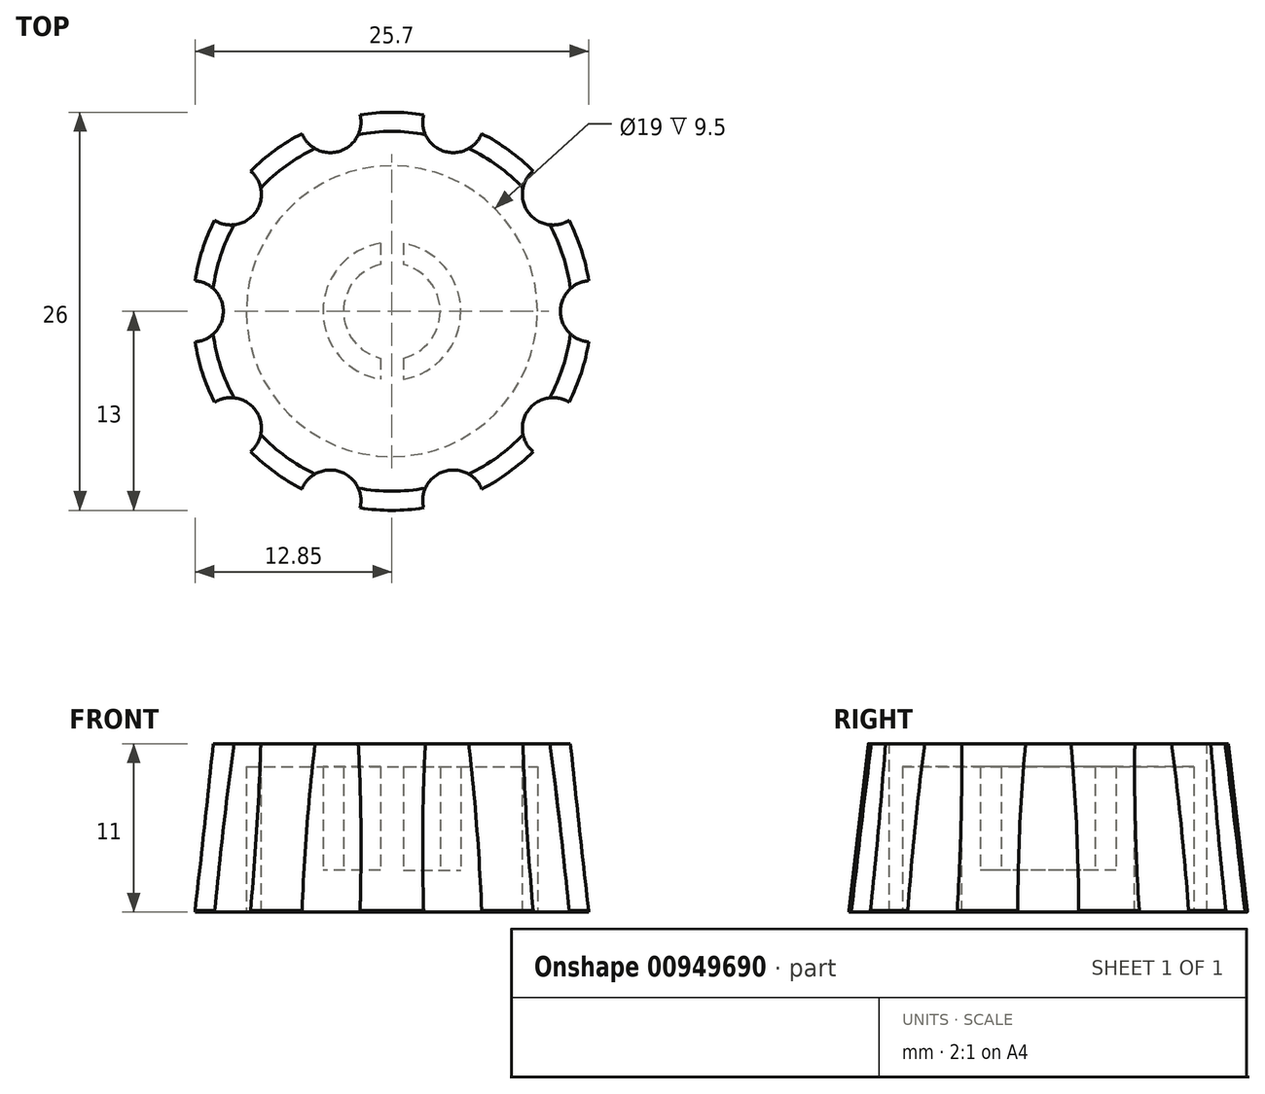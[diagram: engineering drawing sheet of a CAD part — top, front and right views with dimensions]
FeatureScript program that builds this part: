
annotation { "Feature Type Name" : "Feature", "Feature Type Description" : "" }
export const myFeature = defineFeature(function(context is Context, id is Id, definition is map)
    precondition{}
    {
        {
            var Q0;
            Q0=qCreatedBy(makeId("Top.planeOp"),FACE);
            var sketch = newSketch(context, id + "F0", { "sketchPlane" : qUnion([Q0])});
            skCircle(sketch, "E0", {"center": v(0, 0) * mm, "radius": 13 * mm});
            skCircle(sketch, "E1", {"center": v(0, 0) * mm, "radius": 3.15 * mm});
            skCircle(sketch, "E2", {"center": v(0, 0) * mm, "radius": 11.75 * mm});
            skSolve(sketch);
        }
        {
            var Q0;
            Q0=qCreatedBy(makeId("Top.planeOp"),FACE);
            cPlane(context, id + "F1", {"entities" : qUnion([Q0]), "cplaneType" : CPlaneType.OFFSET, "offset" : 11 * mm, "width" : 150 * mm, "height" : 150 * mm});
        }
        {
            var Q0;
            Q0=qCreatedBy(id+"F1.planeOp",FACE);
            var sketch = newSketch(context, id + "F2", { "sketchPlane" : qUnion([Q0])});
            skCircle(sketch, "E3.0", {"center": v(0, 0) * mm, "radius": 11.75 * mm});
            skSolve(sketch);
        }
        {
            var Q0;
            Q0=makeQuery(id+"F0.imprint","IMPRINT",FACE,{"disambiguationData":[TD([[makeQuery(id+"F0.imprint","IMPRINT",EDGE,{"derivedFrom":sQuery(id+"F0.wireOp",EDGE,"E0")}),1.0]])]});
            var Q1;
            Q1=makeQuery(id+"F0.imprint","IMPRINT",FACE,{"disambiguationData":[TD([[makeQuery(id+"F0.imprint","IMPRINT",EDGE,{"derivedFrom":sQuery(id+"F0.wireOp",EDGE,"E1")}),-1.0]])]});
            var Q2;
            Q2=makeQuery(id+"F0.imprint","IMPRINT",FACE,{"disambiguationData":[TD([[makeQuery(id+"F0.imprint","IMPRINT",EDGE,{"derivedFrom":sQuery(id+"F0.wireOp",EDGE,"E1")}),1.0]])]});
            extrude(context, id + "F3", {"entities" : qUnion([Q0, Q1, Q2]), "depth" : 0.1 * mm, "offsetDistance" : 25 * mm});
        }
        {
            var Q1;
            Q1=makeQuery(id+"F3.opExtrude","CAP_FACE",FACE,{"disambiguationData":[OSD([sQuery(id+"F0.wireOp",EDGE,"E0")])],"isStart":false});
            var Q2;
            Q2=makeQuery(id+"F2.imprint","IMPRINT",FACE,{"disambiguationData":[TD([[makeQuery(id+"F2.imprint","IMPRINT",EDGE,{"derivedFrom":sQuery(id+"F2.wireOp",EDGE,"E3.0")}),1.0]])]});
            loft(context, id + "F4", {"operationType" : NewBodyOperationType.ADD, "sheetProfilesArray" : [{ "sheetProfileEntities" : qUnion([Q1]) }, { "sheetProfileEntities" : qUnion([Q2]) }]});
        }
        {
            var Q0;
            Q0=makeQuery(id+"F0.imprint","IMPRINT",FACE,{"disambiguationData":[TD([[makeQuery(id+"F0.imprint","IMPRINT",EDGE,{"derivedFrom":sQuery(id+"F0.wireOp",EDGE,"E1")}),1.0]])]});
            extrude(context, id + "F5", {"entities" : qUnion([Q0]), "operationType" : NewBodyOperationType.REMOVE, "depth" : 9.5 * mm, "offsetDistance" : 25 * mm});
        }
        {
            var Q0;
            Q0=makeQuery(id+"F4.opLoft","CAP_FACE",FACE,{"disambiguationData":[OSD([makeQuery(id+"F2.imprint","IMPRINT",FACE,{"disambiguationData":[TD([[makeQuery(id+"F2.imprint","IMPRINT",EDGE,{"derivedFrom":sQuery(id+"F2.wireOp",EDGE,"E3.0")}),1.0]])]})])],"isStart":true});
            var sketch = newSketch(context, id + "F6", { "sketchPlane" : qUnion([Q0])});
            skCircle(sketch, "E4.0", {"center": v(0, 0) * mm, "radius": 13 * mm, "construction": true});
            skCircle(sketch, "E5", {"center": v(13, 0) * mm, "radius": 2 * mm});
            skCircle(sketch, "E6.1.0", {"center": v(10.52, 7.64) * mm, "radius": 2 * mm});
            skCircle(sketch, "E6.2.0", {"center": v(4.02, 12.36) * mm, "radius": 2 * mm});
            skCircle(sketch, "E6.3.0", {"center": v(-4.02, 12.36) * mm, "radius": 2 * mm});
            skCircle(sketch, "E6.4.0", {"center": v(-10.52, 7.64) * mm, "radius": 2 * mm});
            skCircle(sketch, "E6.5.0", {"center": v(-13, 0) * mm, "radius": 2 * mm});
            skCircle(sketch, "E6.6.0", {"center": v(-10.52, -7.64) * mm, "radius": 2 * mm});
            skCircle(sketch, "E6.7.0", {"center": v(-4.02, -12.36) * mm, "radius": 2 * mm});
            skCircle(sketch, "E6.8.0", {"center": v(4.02, -12.36) * mm, "radius": 2 * mm});
            skCircle(sketch, "E6.9.0", {"center": v(10.52, -7.64) * mm, "radius": 2 * mm});
            skSolve(sketch);
        }
        {
            var Q0;
            Q0 = qSketchRegion(id + "F6", true);
            extrude(context, id + "F7", {"entities" : qUnion([Q0]), "operationType" : NewBodyOperationType.REMOVE, "oppositeDirection" : true, "depth" : 25 * mm, "offsetDistance" : 25 * mm});
        }
        {
            var Q0;
            Q0 = qSketchRegion(id + "F6", true);
            extrude(context, id + "F8", {"entities" : qUnion([Q0]), "operationType" : NewBodyOperationType.REMOVE, "endBound" : BoundingType.THROUGH_ALL, "oppositeDirection" : true, "depth" : 4 * mm, "offsetDistance" : 25 * mm});
        }
        {
            var Q0;
            Q0=makeQuery(id+"F3.opExtrude","CAP_FACE",FACE,{"disambiguationData":[OSD([sQuery(id+"F0.wireOp",EDGE,"E0")])],"isStart":true});
            var sketch = newSketch(context, id + "F9", { "sketchPlane" : qUnion([Q0])});
            skCircle(sketch, "E7", {"center": v(0, 0) * mm, "radius": 9.5 * mm});
            skArc(sketch, "E8", {"start": v(0.75, -4.44) * mm, "mid": v(4.5, 0) * mm, "end": v(0.75, 4.44) * mm});
            skArc(sketch, "E9.0", {"start": v(0.75, -3.06) * mm, "mid": v(3.15, 0) * mm, "end": v(0.75, 3.06) * mm});
            skLineSegment(sketch, "E10.left", {"start": v(0.75, -4.44) * mm, "end": v(0.75, -3.06) * mm});
            skLineSegment(sketch, "E10.right", {"start": v(-0.75, -4.44) * mm, "end": v(-0.75, -3.06) * mm});
            skLineSegment(sketch, "E11.trimOffspring", {"start": v(0.75, 3.06) * mm, "end": v(0.75, 4.44) * mm});
            skLineSegment(sketch, "E12.trimOffspring", {"start": v(-0.75, 3.06) * mm, "end": v(-0.75, 4.44) * mm});
            skArc(sketch, "E13.trimOffspring", {"start": v(-0.75, 3.06) * mm, "mid": v(-3.15, 0) * mm, "end": v(-0.75, -3.06) * mm});
            skArc(sketch, "E14.trimOffspring", {"start": v(-0.75, 4.44) * mm, "mid": v(-4.5, 0) * mm, "end": v(-0.75, -4.44) * mm});
            skArc(sketch, "E15.0", {"start": v(-0.75, -3.06) * mm, "mid": v(0, -3.15) * mm, "end": v(0.75, -3.06) * mm});
            skArc(sketch, "E16.trimOffspring", {"start": v(0.75, 3.06) * mm, "mid": v(0, 3.15) * mm, "end": v(-0.75, 3.06) * mm});
            skSolve(sketch);
        }
        {
            var Q0;
            Q0=makeQuery(id+"F9.imprint","IMPRINT",FACE,{"disambiguationData":[TD([[makeQuery(id+"F9.imprint","IMPRINT",EDGE,{"derivedFrom":sQuery(id+"F9.wireOp",EDGE,"E7")}),1.0]])]});
            extrude(context, id + "F10", {"entities" : qUnion([Q0]), "operationType" : NewBodyOperationType.REMOVE, "oppositeDirection" : true, "depth" : 9.5 * mm, "offsetDistance" : 25 * mm});
        }
        {
            var Q0;
            Q0=makeQuery(id+"F10.boolean.opBoolean","SPLIT",FACE,{"disambiguationData":[TD([makeQuery(id+"F10.opExtrude","SWEPT_FACE",FACE,{"disambiguationData":[OSD([sQuery(id+"F9.wireOp",EDGE,"E10.right")])]})])],"derivedFrom":makeQuery(id+"F3.opExtrude","CAP_FACE",FACE,{"disambiguationData":[OSD([sQuery(id+"F0.wireOp",EDGE,"E0")])],"isStart":true})});
            var Q1;
            Q1=makeQuery(id+"F10.boolean.opBoolean","SPLIT",FACE,{"disambiguationData":[TD([makeQuery(id+"F10.opExtrude","SWEPT_FACE",FACE,{"disambiguationData":[OSD([sQuery(id+"F9.wireOp",EDGE,"E8")])]})])],"derivedFrom":makeQuery(id+"F3.opExtrude","CAP_FACE",FACE,{"disambiguationData":[OSD([sQuery(id+"F0.wireOp",EDGE,"E0")])],"isStart":true})});
            extrude(context, id + "F11", {"entities" : qUnion([Q0, Q1]), "operationType" : NewBodyOperationType.REMOVE, "oppositeDirection" : true, "depth" : 2.75 * mm, "offsetDistance" : 25 * mm});
        }
    });
